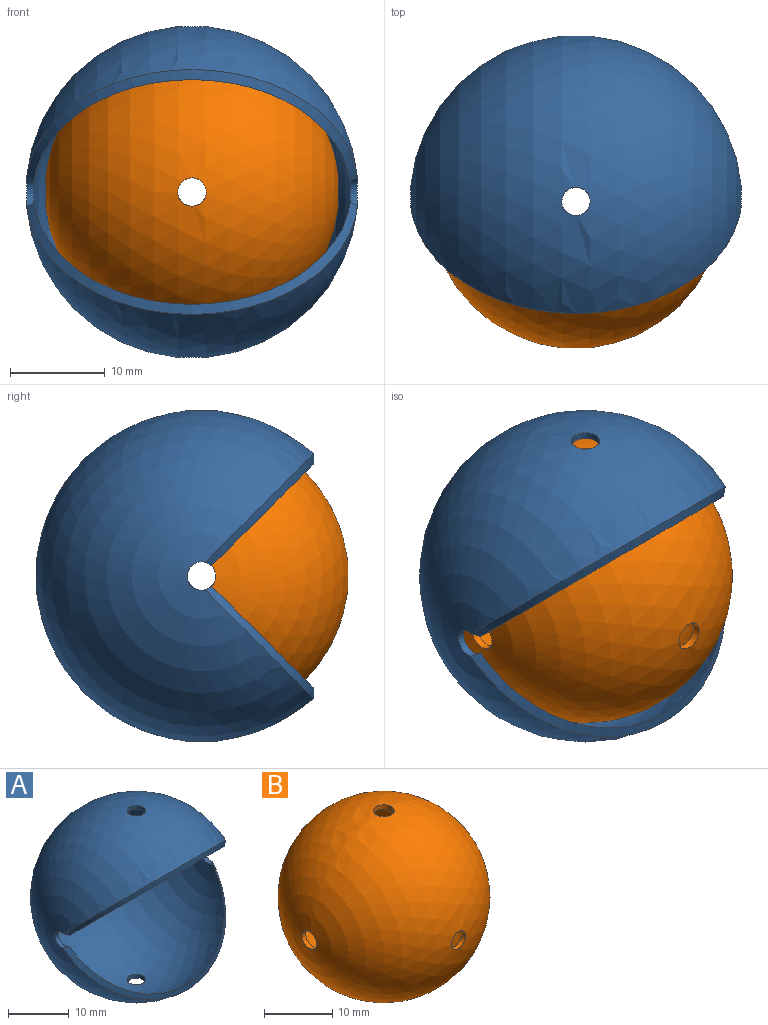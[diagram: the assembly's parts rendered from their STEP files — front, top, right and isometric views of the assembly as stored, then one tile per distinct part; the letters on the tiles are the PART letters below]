
ASSEMBLY  parts=2 mates=1
PART A: 9 faces, bbox 34.9x29.3x35 mm
  f0: sphere r=17.5mm, area 2774.2mm2, adj f2,f3,f4,f5,f6,f7,f8
  f1: sphere r=16.75mm, area 2611.5mm2, adj f2,f3,f4,f5,f6,f7,f8
  f2: cylinder r=1.5mm len=3mm, axis (1,0,0), area 4.7mm2, adj f0,f1,f7,f8
  f3: cylinder r=1.5mm len=3mm, axis (-1,0,0), area 4.7mm2, adj f0,f1,f7,f8
  f4: cylinder r=1.5mm len=3mm, axis (0,-1,0), area 7.1mm2, adj f0,f1
  f5: cylinder r=1.5mm len=3mm, axis (0,0,1), area 7.1mm2, adj f0,f1
  f6: cylinder r=1.5mm len=3mm, axis (0,0,-1), area 7.1mm2, adj f0,f1
  f7: cone r=17.48mm half-angle=43.7deg, axis (0,0.71,-0.71), area 54mm2, adj f0,f1,f2,f3
  f8: cone r=16.75mm half-angle=43.7deg, axis (0,0.71,0.71), area 54mm2, adj f0,f1,f2,f3
PART B: 8 faces, bbox 30.9x31x31 mm
  f0: sphere r=15.5mm, area 2976.6mm2, adj f2,f3,f4,f5,f6,f7
  f1: sphere r=14.75mm, area 2691.5mm2, adj f2,f3,f4,f5,f6,f7
  f2: cylinder r=1.5mm len=3mm, axis (0,0,1), area 7.1mm2, adj f0,f1
  f3: cylinder r=1.5mm len=3mm, axis (0,0,-1), area 7.1mm2, adj f0,f1
  f4: cylinder r=1.5mm len=3mm, axis (1,0,0), area 7.1mm2, adj f0,f1
  f5: cylinder r=1.5mm len=3mm, axis (-1,0,0), area 7.1mm2, adj f0,f1
  f6: cylinder r=1.5mm len=3mm, axis (0,-1,0), area 7.1mm2, adj f0,f1
  f7: cylinder r=1.5mm len=3mm, axis (0,1,0), area 7.1mm2, adj f0,f1
PLACE A t=(-25.91,5.59,-0.04)mm
PLACE B t=(-25.91,5.6,-0.04)mm
MATE ball A.f5 <-> B.f2  axis (0,0,1) through (-25.91,5.6,-0.04)mm
